# Revit family: Trigon_CB-353_BIM
name_source: partatom
category: Arredi
units: mm (PartAtom-declared; Revit-internal decimal feet)

## family parameters
Attiva taglio nelle viste = No
Basato su piano di lavoro = No
Condiviso = No
Numero OmniClass = 23.40.20.00
Origine composizione di rendering = Geometria famiglia
Punto di calcolo locali = No
Sempre verticale = Sì
Taglio con vuoti quando caricato = No
Titolo OmniClass = General Furniture and Specialties

## types (1)
- CB-353
    AVAILABLE FINISHES = Satin nickel (SN), satin brass (SB), bronze (BZ) or gunmetal (GM) nanoceramic coating.
    BASE MATERIAL = BASSAM_FELLOWS_BRONZE_BZ
    BIM BADGE = https://bim.archiproducts.com
    COLLECTION = Trigon
    DEPTH = 364 mm  [stored 1.19423 ft]
    Descrizione = Steel side table
    HEIGHT = 563 mm  [stored 1.84711 ft]
    MATERIAL DESCRIPTION = Steel plate top and base with tubular steel pedestal.
    Modello = Trigon Pedestal Side Table
    PRODUCT CODE = CB-353
    PRODUCT SHEET = https://www.archiproducts.com
    Produttore = BassamFellows
    Prospetto di default = 0 mm  [stored 0 ft]
    TECHNICAL SHEET = https://bassamfellows.com
    URL = https://bassamfellows.com
    WIDTH = 373 mm  [stored 1.22375 ft]

note: [stored X ft] marks values corroborated as IEEE doubles in the binary element streams (Revit-internal decimal feet)

## geometry (parser evidence)
native form markers: Sweep x1
no freeform markers — native parametric forms only
